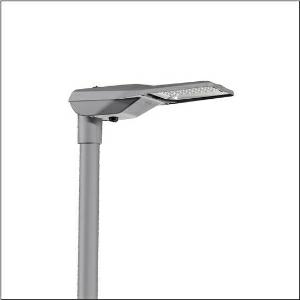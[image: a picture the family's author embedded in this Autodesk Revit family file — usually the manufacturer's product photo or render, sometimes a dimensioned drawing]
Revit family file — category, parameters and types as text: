
# Revit family: streetlight_sl_21_mini___stw1_0a_5xe2e33t08jb_e144
name_source: partatom
category: Lighting Fixtures
units: mm (PartAtom-declared; Revit-internal decimal feet)

## family parameters
Cut with Voids When Loaded = No
Host = Face
Light Source = No
Part Type = Normal
Room Calculation Point = No
Round Connector Dimension = Use Diameter
Shared = No

## types (1)
- --- (1 x LED, 12940 lm, 88.6 W, 3000K)
    Apparent Load = 89 VA
    CIE Flux Codes = 39 75 98 100 100
    Color Rendering = 70
    Color Temperature = 3000K
    Default Elevation = 1800 mm
    Description = Streetlight SL 21 mini, mast luminaire, primary light control with lens, of PMMA, primary optical cover: cover, of toughened safety glass, transparent, light distribution: STW1.0a, light emission: direct distribution, primary light characteristic: asymmetric, installation type: side-entry, post-top, LED, High Power LED, rated luminous flux: 12.940lm, luminous efficacy: 146lm/W, light colour: 730, colour temperature: 3000K, control gear: D4i, control: overheat protection, constant luminous flux control, time-dependent luminous flux control, flexible luminous flux parameterisation, pre-setting: logarithmic dimming characteristic, mains connection: 220..240V, AC, 50/60Hz, start of lifetime: 89W, end of service life: 92W, reduction: 41W, luminaire housing, of diecast aluminium, powder-coated, Siteco® metallic grey (DB 702S), corrosivity category C5 mid according to DIN EN ISO 12944, please order mast flange separately, inclination adjustable: 0°, 5°, 10°, 15°, sealing non-destructively replaceable, multi-level sealing system, length: 628mm, width: 235mm, height: 110mm, mast flange for spigot size: 42mm (side-entry): 5XC10008XM4, 60/48mm (side-entry/post-top): 5XC10108XM2, 76/60mm (side-entry/post-top): 5XC10108XM1, mounting height: 4..8m, Smart Interface below and above, protection rating (complete): IP66, insulation class (complete): insulation class II (safety insulation), certification: CE, ENEC, ENEC+, VDE, impact resistance: IK10, permissible operating ambient temperature for outdoor applications: -40..+50°C, standard-compliant lighting for roads and squares, packaging unit: 1 piece

Light Distribution: STW1.0a
    Height = 110 mm
    Lamp = 1 x LED
    Lamp Light Flux = 12940 lm
    Lamp Power = 88.6 W
    Lamp count = 1
    Length = 625 mm
    Luminous efficacy = 146 lm/W
    Manufacturer = Siteco
    ModVariant = No
    Model = 5XE2E33T08JB
    Number of Poles = 1
    OnlyDefault = Yes
    Power Factor = 1
    Product Name = Streetlight SL 21 mini | STW1.0a
    Product group = mast luminaire | pylon top
    ProductGroupID = 6100
    Protection Class = Protection class II
    Protection Degree = IP 66
    RLX_Detail_Level = 1
    RLX_Emergency_Light_Flux = 0 lm
    RLX_Emergency_Type = 0
    RLX_Emergency_Type_DB = No
    RlxData = <blob elided: 26481 chars, md5=3d755b45>
    Socket = socket
    Standby Power = 0 W
    System Light Flux = 12940 lm
    System Power = 89 W
    Type Comments = factory setting: luminous flux: 100 % | dim-lin: 254 | 915 mA
    Type Image = l_1003514.jpg
    URL = http://relux.com
    VarID = @adj_031325
    Voltage = 0 V
    Weight = 0.00 kg
    Width = 234 mm

## geometry (parser evidence)
native form markers: Blend x4, Sweep x11
no freeform markers — native parametric forms only
